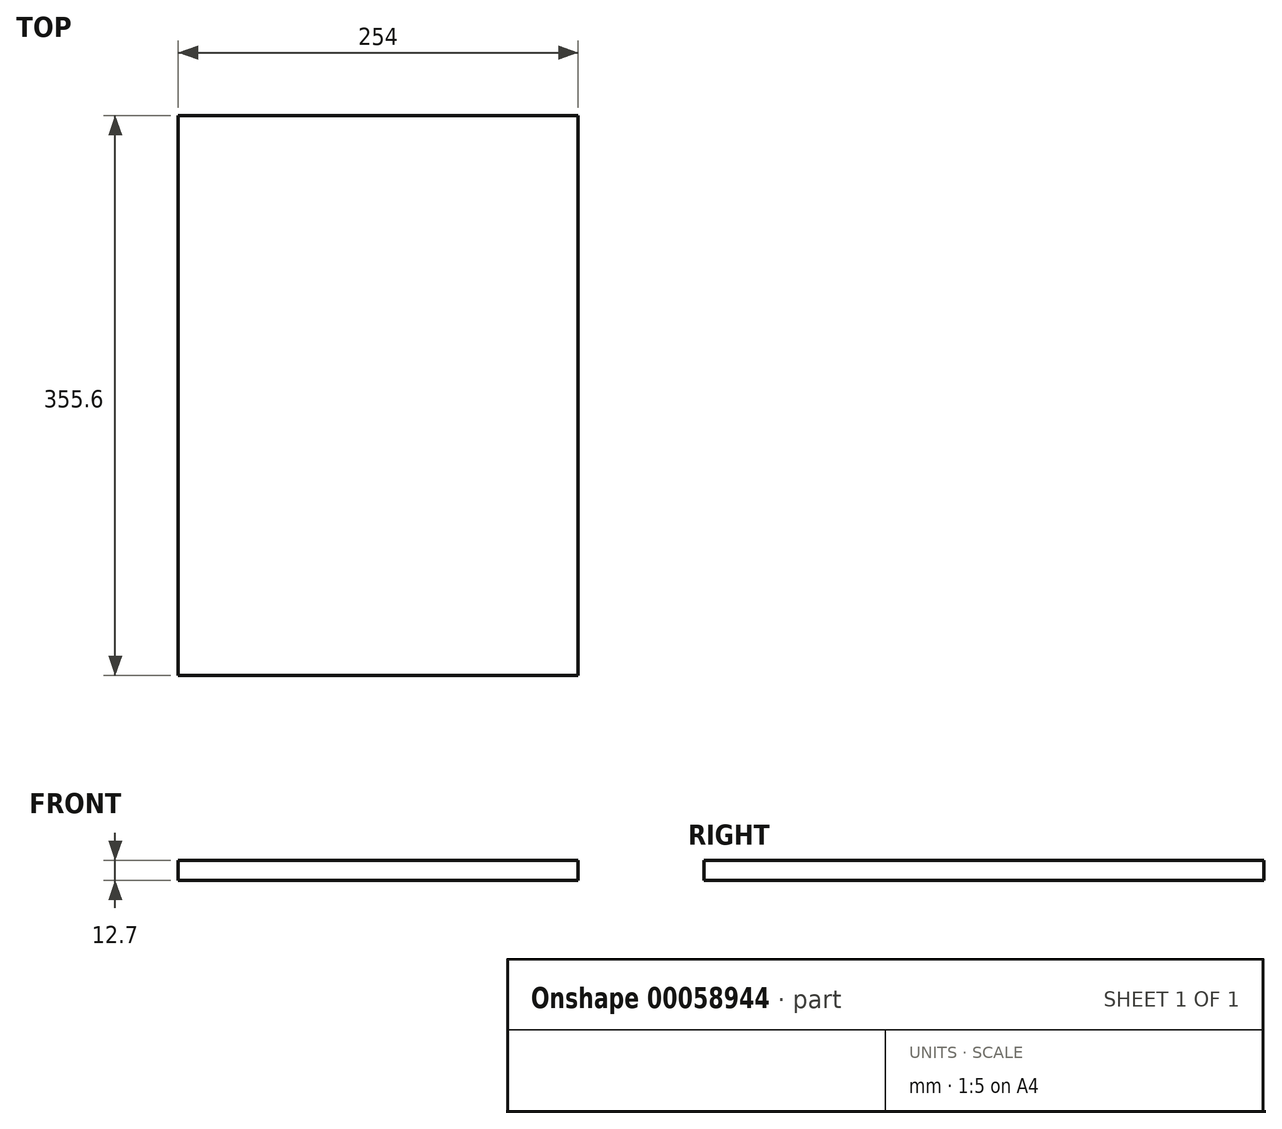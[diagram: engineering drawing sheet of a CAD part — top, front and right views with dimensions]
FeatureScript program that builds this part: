
annotation { "Feature Type Name" : "Feature", "Feature Type Description" : "" }
export const myFeature = defineFeature(function(context is Context, id is Id, definition is map)
    precondition{}
    {
        {
            var Q0;
            Q0=qCreatedBy(makeId("Top.planeOp"),FACE);
            var sketch = newSketch(context, id + "F0", { "sketchPlane" : qUnion([Q0])});
            skLineSegment(sketch, "E0.bottom", {"start": v(-127, -177.8) * mm, "end": v(127, -177.8) * mm});
            skLineSegment(sketch, "E0.top", {"start": v(-127, 177.8) * mm, "end": v(127, 177.8) * mm});
            skLineSegment(sketch, "E0.left", {"start": v(-127, -177.8) * mm, "end": v(-127, 177.8) * mm});
            skLineSegment(sketch, "E0.right", {"start": v(127, -177.8) * mm, "end": v(127, 177.8) * mm});
            skLineSegment(sketch, "E1", {"start": v(0, -177.8) * mm, "end": v(0, 177.8) * mm});
            skLineSegment(sketch, "E2", {"start": v(-127, 0) * mm, "end": v(127, 0) * mm});
            skPoint(sketch, "E3", {"position": v(0, 0) * mm});
            skSolve(sketch);
        }
        {
            var Q0;
            Q0 = qSketchRegion(id + "F0", true);
            extrude(context, id + "F1", {"entities" : qUnion([Q0]), "depth" : 12.7 * mm});
        }
    });
